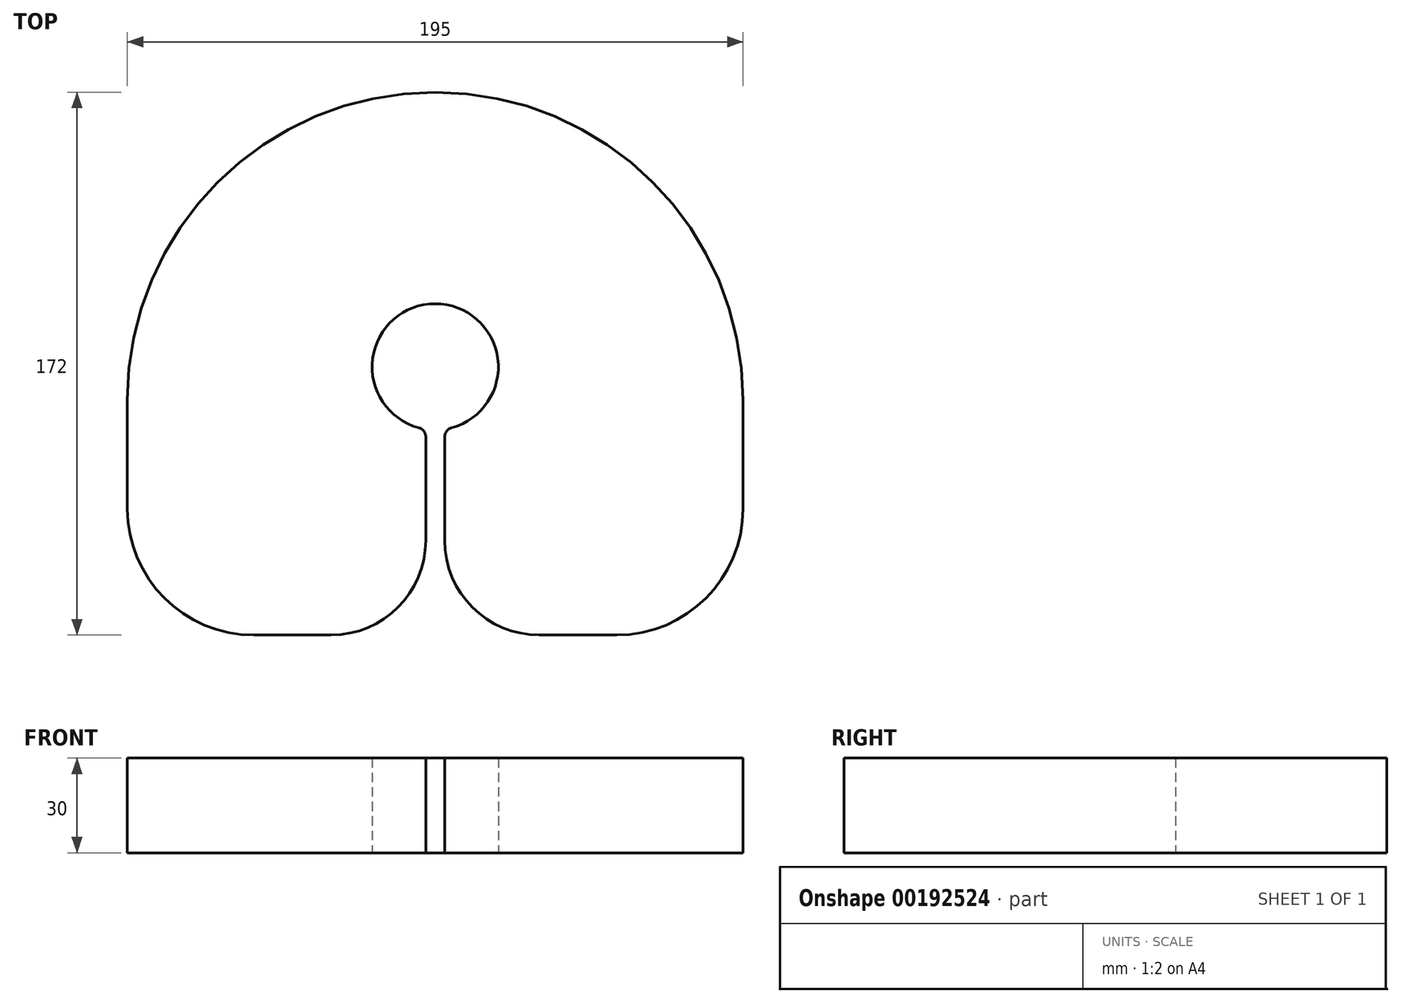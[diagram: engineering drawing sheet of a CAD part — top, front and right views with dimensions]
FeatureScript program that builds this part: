
annotation { "Feature Type Name" : "Feature", "Feature Type Description" : "" }
export const myFeature = defineFeature(function(context is Context, id is Id, definition is map)
    precondition{}
    {
        {
            var Q0;
            Q0=qCreatedBy(makeId("Top.planeOp"),FACE);
            var sketch = newSketch(context, id + "F0", { "sketchPlane" : qUnion([Q0])});
            skLineSegment(sketch, "E0", {"start": v(-97.5, -45) * mm, "end": v(-97.5, -10.5) * mm});
            skLineSegment(sketch, "E1", {"start": v(97.5, -10.5) * mm, "end": v(97.5, -45) * mm});
            skArc(sketch, "E2", {"start": v(97.5, -45) * mm, "mid": v(85.78, -73.28) * mm, "end": v(57.5, -85) * mm});
            skArc(sketch, "E3", {"start": v(-97.5, -45) * mm, "mid": v(-85.78, -73.28) * mm, "end": v(-57.5, -85) * mm});
            skLineSegment(sketch, "E4", {"start": v(-57.5, -85) * mm, "end": v(-33, -85) * mm});
            skLineSegment(sketch, "E5", {"start": v(57.5, -85) * mm, "end": v(33, -85) * mm});
            skArc(sketch, "E6", {"start": v(-33, -85) * mm, "mid": v(-11.79, -76.21) * mm, "end": v(-3, -55) * mm});
            skArc(sketch, "E7", {"start": v(33, -85) * mm, "mid": v(11.79, -76.21) * mm, "end": v(3, -55) * mm});
            skLineSegment(sketch, "E8", {"start": v(3, -55) * mm, "end": v(3, -22.2) * mm});
            skLineSegment(sketch, "E9", {"start": v(-3, -55) * mm, "end": v(-3, -22.2) * mm});
            skArc(sketch, "E10", {"start": v(5.22, -19.3) * mm, "mid": v(0, 20) * mm, "end": v(-5.22, -19.3) * mm});
            skPoint(sketch, "E11.visualSharp", {"position": v(-3, -19.77) * mm});
            skArc(sketch, "E11.filletArc", {"start": v(-3, -22.2) * mm, "mid": v(-3.62, -20.38) * mm, "end": v(-5.22, -19.3) * mm});
            skPoint(sketch, "E12.visualSharp", {"position": v(3, -19.77) * mm});
            skArc(sketch, "E12.filletArc", {"start": v(5.22, -19.3) * mm, "mid": v(3.62, -20.38) * mm, "end": v(3, -22.2) * mm});
            skArc(sketch, "E13", {"start": v(97.5, -10.5) * mm, "mid": v(0, 87) * mm, "end": v(-97.5, -10.5) * mm});
            skSolve(sketch);
        }
        {
            var Q0;
            Q0 = qSketchRegion(id + "F0", true);
            var Q1;
            Q1 = qConstructionFilter(qBodyType(qCreatedBy(id + "F0" ,EDGE), BodyType.WIRE), ConstructionObject.NO);
            extrude(context, id + "F1", {"entities" : qUnion([Q0]), "surfaceEntities" : qUnion([Q1]), "depth" : 30 * mm});
        }
    });
